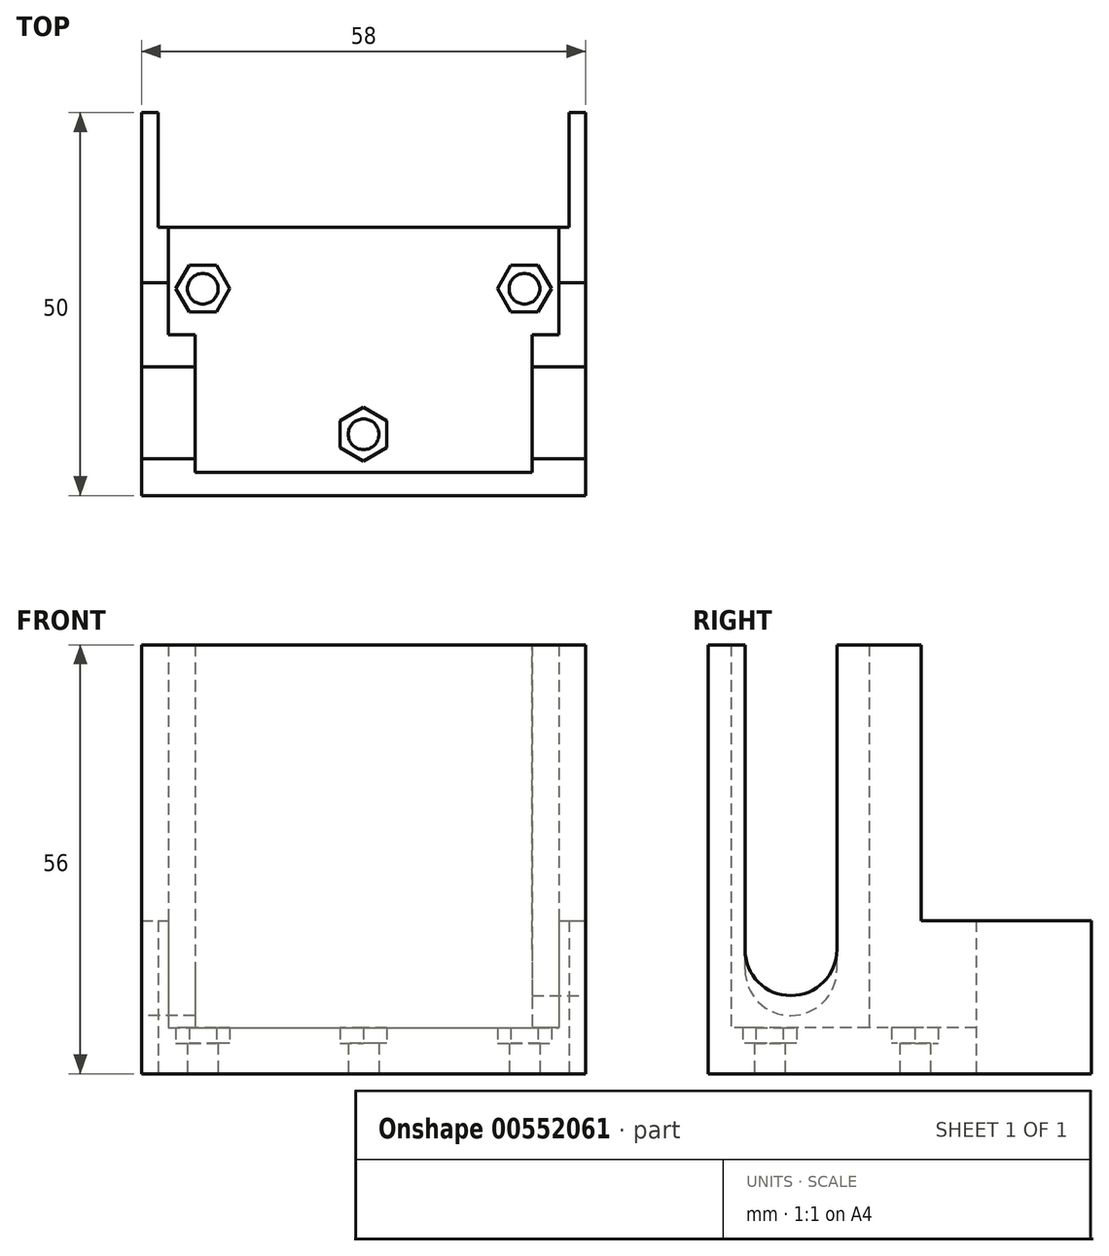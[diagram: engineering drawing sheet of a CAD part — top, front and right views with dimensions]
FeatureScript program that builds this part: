
annotation { "Feature Type Name" : "Feature", "Feature Type Description" : "" }
export const myFeature = defineFeature(function(context is Context, id is Id, definition is map)
    precondition{}
    {
        {
            var Q0;
            Q0=qCreatedBy(makeId("Top.planeOp"),FACE);
            var sketch = newSketch(context, id + "F0", { "sketchPlane" : qUnion([Q0])});
            skLineSegment(sketch, "E0.bottom", {"start": v(-26.85, 17.5) * mm, "end": v(26.85, 17.5) * mm});
            skLineSegment(sketch, "E0.top", {"start": v(-29, -17.5) * mm, "end": v(29, -17.5) * mm});
            skLineSegment(sketch, "E0.left", {"start": v(-29, 17.5) * mm, "end": v(-29, -17.5) * mm});
            skLineSegment(sketch, "E0.right", {"start": v(29, 17.5) * mm, "end": v(29, -17.5) * mm});
            skLineSegment(sketch, "E1.top", {"start": v(-29, 32.5) * mm, "end": v(-26.85, 32.5) * mm});
            skLineSegment(sketch, "E1.left", {"start": v(-29, 17.5) * mm, "end": v(-29, 32.5) * mm});
            skLineSegment(sketch, "E1.right", {"start": v(-26.85, 17.5) * mm, "end": v(-26.85, 32.5) * mm});
            skLineSegment(sketch, "E2.MirrorCS", {"start": v(29, 32.5) * mm, "end": v(26.85, 32.5) * mm});
            skLineSegment(sketch, "E3.MirrorCS", {"start": v(26.85, 17.5) * mm, "end": v(26.85, 32.5) * mm});
            skLineSegment(sketch, "E4.MirrorCS", {"start": v(29, 17.5) * mm, "end": v(29, 32.5) * mm});
            skCircle(sketch, "E5", {"center": v(-21, 9.5) * mm, "radius": 2 * mm});
            skCircle(sketch, "E6.MirrorC", {"center": v(21, 9.5) * mm, "radius": 2 * mm});
            skCircle(sketch, "E7.MirrorC", {"center": v(0, -9.5) * mm, "radius": 2 * mm});
            skSolve(sketch);
        }
        {
            var Q0;
            Q0 = qSketchRegion(id + "F0", true);
            extrude(context, id + "F1", {"entities" : qUnion([Q0]), "depth" : 4 * mm, "offsetDistance" : 25 * mm});
        }
        {
            var Q0;
            Q0=makeQuery(id+"F1.opExtrude","CAP_FACE",FACE,{"disambiguationData":[OSD([sQuery(id+"F0.wireOp",EDGE,"E0.bottom"),sQuery(id+"F0.wireOp",EDGE,"E0.top"),sQuery(id+"F0.wireOp",EDGE,"E0.left"),sQuery(id+"F0.wireOp",EDGE,"E0.right"),sQuery(id+"F0.wireOp",EDGE,"E1.top"),sQuery(id+"F0.wireOp",EDGE,"E1.left"),sQuery(id+"F0.wireOp",EDGE,"E1.right"),sQuery(id+"F0.wireOp",EDGE,"E2.MirrorCS"),sQuery(id+"F0.wireOp",EDGE,"E3.MirrorCS"),sQuery(id+"F0.wireOp",EDGE,"E4.MirrorCS"),sQuery(id+"F0.wireOp",EDGE,"E5"),sQuery(id+"F0.wireOp",EDGE,"E6.MirrorC"),sQuery(id+"F0.wireOp",EDGE,"E7.MirrorC"),sQuery(id+"F0.wireOp",EDGE,"1b375347-9f48-4c3b-9e81-8c62cc754c121.MirrorC")])],"isStart":false});
            var sketch = newSketch(context, id + "F2", { "sketchPlane" : qUnion([Q0])});
            skCircle(sketch, "E8.cCircle", {"center": v(-21, 9.5) * mm, "radius": 3.05 * mm, "construction": true});
            skLineSegment(sketch, "E8.0", {"start": v(-19.24, 6.45) * mm, "end": v(-22.76, 6.45) * mm});
            skLineSegment(sketch, "E8.1", {"start": v(-22.76, 6.45) * mm, "end": v(-24.52, 9.5) * mm});
            skLineSegment(sketch, "E8.2", {"start": v(-24.52, 9.5) * mm, "end": v(-22.76, 12.55) * mm});
            skLineSegment(sketch, "E8.3", {"start": v(-22.76, 12.55) * mm, "end": v(-19.24, 12.55) * mm});
            skLineSegment(sketch, "E8.4", {"start": v(-19.24, 12.55) * mm, "end": v(-17.48, 9.5) * mm});
            skLineSegment(sketch, "E8.5", {"start": v(-17.48, 9.5) * mm, "end": v(-19.24, 6.45) * mm});
            skPoint(sketch, "E8.0.midPoint", {"position": v(-21, 6.45) * mm});
            skLineSegment(sketch, "E9.MirrorCS", {"start": v(24.52, 9.5) * mm, "end": v(22.76, 12.55) * mm});
            skLineSegment(sketch, "E10.MirrorCS", {"start": v(17.48, 9.5) * mm, "end": v(19.24, 6.45) * mm});
            skPoint(sketch, "E11.MirrorP", {"position": v(21, 6.45) * mm});
            skCircle(sketch, "E12.MirrorC", {"center": v(21, 9.5) * mm, "radius": 3.05 * mm, "construction": true});
            skLineSegment(sketch, "E13.MirrorCS", {"start": v(19.24, 6.45) * mm, "end": v(22.76, 6.45) * mm});
            skLineSegment(sketch, "E14.MirrorCS", {"start": v(22.76, 6.45) * mm, "end": v(24.52, 9.5) * mm});
            skLineSegment(sketch, "E15.MirrorCS", {"start": v(22.76, 12.55) * mm, "end": v(19.24, 12.55) * mm});
            skLineSegment(sketch, "E16.MirrorCS", {"start": v(19.24, 12.55) * mm, "end": v(17.48, 9.5) * mm});
            skCircle(sketch, "E17.cCircle", {"center": v(0, -9.5) * mm, "radius": 3.05 * mm, "construction": true});
            skLineSegment(sketch, "E17.0", {"start": v(0, -13.02) * mm, "end": v(-3.05, -11.26) * mm});
            skLineSegment(sketch, "E17.1", {"start": v(-3.05, -11.26) * mm, "end": v(-3.05, -7.74) * mm});
            skLineSegment(sketch, "E17.2", {"start": v(-3.05, -7.74) * mm, "end": v(0, -5.98) * mm});
            skLineSegment(sketch, "E17.3", {"start": v(0, -5.98) * mm, "end": v(3.05, -7.74) * mm});
            skLineSegment(sketch, "E17.4", {"start": v(3.05, -7.74) * mm, "end": v(3.05, -11.26) * mm});
            skLineSegment(sketch, "E17.5", {"start": v(3.05, -11.26) * mm, "end": v(0, -13.02) * mm});
            skPoint(sketch, "E17.0.midPoint", {"position": v(-1.53, -12.14) * mm});
            skSolve(sketch);
        }
        {
            var Q0;
            Q0=makeQuery(id+"F2.imprint","IMPRINT",FACE,{"disambiguationData":[TD([[makeQuery(id+"F2.imprint","IMPRINT",EDGE,{"derivedFrom":sQuery(id+"F2.wireOp",EDGE,"E8.0")}),1.0]])]});
            extrude(context, id + "F3", {"entities" : qUnion([Q0]), "operationType" : NewBodyOperationType.ADD, "depth" : 2 * mm, "offsetDistance" : 25 * mm});
        }
        {
            var Q0;
            Q0=makeQuery(id+"F3.opExtrude","CAP_FACE",FACE,{"disambiguationData":[OSD([sQuery(id+"F0.wireOp",EDGE,"E0.bottom"),sQuery(id+"F0.wireOp",EDGE,"E0.top"),sQuery(id+"F0.wireOp",EDGE,"E0.left"),sQuery(id+"F0.wireOp",EDGE,"E0.right"),sQuery(id+"F0.wireOp",EDGE,"E1.top"),sQuery(id+"F0.wireOp",EDGE,"E1.left"),sQuery(id+"F0.wireOp",EDGE,"E1.right"),sQuery(id+"F0.wireOp",EDGE,"E2.MirrorCS"),sQuery(id+"F0.wireOp",EDGE,"E3.MirrorCS"),sQuery(id+"F0.wireOp",EDGE,"E4.MirrorCS"),sQuery(id+"F2.wireOp",EDGE,"E8.0"),sQuery(id+"F2.wireOp",EDGE,"E8.1"),sQuery(id+"F2.wireOp",EDGE,"E8.2"),sQuery(id+"F2.wireOp",EDGE,"E8.3"),sQuery(id+"F2.wireOp",EDGE,"E8.4"),sQuery(id+"F2.wireOp",EDGE,"E8.5"),sQuery(id+"F2.wireOp",EDGE,"E9.MirrorCS"),sQuery(id+"F2.wireOp",EDGE,"E10.MirrorCS"),sQuery(id+"F2.wireOp",EDGE,"E13.MirrorCS"),sQuery(id+"F2.wireOp",EDGE,"E14.MirrorCS"),sQuery(id+"F2.wireOp",EDGE,"E15.MirrorCS"),sQuery(id+"F2.wireOp",EDGE,"E16.MirrorCS"),sQuery(id+"F2.wireOp",EDGE,"72694715-5b62-4953-aa1a-f60ba5feefbf0.MirrorCS"),sQuery(id+"F2.wireOp",EDGE,"72694715-5b62-4953-aa1a-f60ba5feefbf1.MirrorCS"),sQuery(id+"F2.wireOp",EDGE,"72694715-5b62-4953-aa1a-f60ba5feefbf2.MirrorCS"),sQuery(id+"F2.wireOp",EDGE,"72694715-5b62-4953-aa1a-f60ba5feefbf3.MirrorCS"),sQuery(id+"F2.wireOp",EDGE,"72694715-5b62-4953-aa1a-f60ba5feefbf4.MirrorCS"),sQuery(id+"F2.wireOp",EDGE,"72694715-5b62-4953-aa1a-f60ba5feefbf8.MirrorCS"),sQuery(id+"F2.wireOp",EDGE,"72694715-5b62-4953-aa1a-f60ba5feefbf9.MirrorCS"),sQuery(id+"F2.wireOp",EDGE,"72694715-5b62-4953-aa1a-f60ba5feefbf11.MirrorCS"),sQuery(id+"F2.wireOp",EDGE,"72694715-5b62-4953-aa1a-f60ba5feefbf12.MirrorCS"),sQuery(id+"F2.wireOp",EDGE,"72694715-5b62-4953-aa1a-f60ba5feefbf13.MirrorCS"),sQuery(id+"F2.wireOp",EDGE,"72694715-5b62-4953-aa1a-f60ba5feefbf14.MirrorCS"),sQuery(id+"F2.wireOp",EDGE,"72694715-5b62-4953-aa1a-f60ba5feefbf15.MirrorCS")])],"isStart":false});
            var sketch = newSketch(context, id + "F4", { "sketchPlane" : qUnion([Q0])});
            skLineSegment(sketch, "E18", {"start": v(-25.5, 17.5) * mm, "end": v(-25.5, 3.5) * mm});
            skLineSegment(sketch, "E19.MirrorCS", {"start": v(25.5, 17.5) * mm, "end": v(25.5, 3.5) * mm});
            skLineSegment(sketch, "E20", {"start": v(-22, -14.5) * mm, "end": v(22, -14.5) * mm});
            skLineSegment(sketch, "E21.bottom", {"start": v(-25.5, 3.5) * mm, "end": v(-22, 3.5) * mm});
            skLineSegment(sketch, "E21.right", {"start": v(-22, 3.5) * mm, "end": v(-22, -14.5) * mm});
            skLineSegment(sketch, "E22.MirrorCS", {"start": v(22, 3.5) * mm, "end": v(22, -14.5) * mm});
            skLineSegment(sketch, "E23.MirrorCS", {"start": v(25.5, 3.5) * mm, "end": v(22, 3.5) * mm});
            skSolve(sketch);
        }
        {
            var Q0;
            Q0 = qSketchRegion(id + "F4", true);
            var Q1;
            {var subQ2=sQuery(id+"F4.wireOp",EDGE,"E18");Q1=makeQuery(id+"F4.imprint","IMPRINT",FACE,{"disambiguationData":[TD([[makeQuery(id+"F4.imprint","IMPRINT",EDGE,{"derivedFrom":subQ2}),-1.0]])]});}
            extrude(context, id + "F5", {"entities" : qUnion([Q0, Q1]), "operationType" : NewBodyOperationType.ADD, "depth" : 50 * mm, "offsetDistance" : 25 * mm});
        }
        {
            var Q0;
            {var subQ0=sQuery(id+"F0.wireOp",EDGE,"E1.left");var subQ1=sQuery(id+"F0.wireOp",EDGE,"E0.left");Q0=makeQuery(id+"F5.boolean.opBoolean","MERGE",FACE,{"derivedFrom":[makeQuery(id+"F3.boolean.opBoolean","MERGE",FACE,{"derivedFrom":[makeQuery(id+"F1.opExtrude","SWEPT_FACE",FACE,{"disambiguationData":[OSD([subQ1,subQ0])]}),makeQuery(id+"F3.opExtrude","SWEPT_FACE",FACE,{"disambiguationData":[OSD([subQ1,subQ0])]})]}),makeQuery(id+"F5.opExtrude","SWEPT_FACE",FACE,{"disambiguationData":[OSD([subQ1,subQ0])]})]});}
            var sketch = newSketch(context, id + "F6", { "sketchPlane" : qUnion([Q0])});
            skArc(sketch, "E24", {"start": v(0.7, 13.6) * mm, "mid": v(6.7, 7.6) * mm, "end": v(12.7, 13.6) * mm});
            skLineSegment(sketch, "E25", {"start": v(12.7, 13.6) * mm, "end": v(12.7, 56) * mm});
            skLineSegment(sketch, "E26", {"start": v(0.7, 13.6) * mm, "end": v(0.7, 56) * mm});
            skSolve(sketch);
        }
        {
            var Q0;
            Q0 = qSketchRegion(id + "F6", true);
            var Q1;
            Q1=makeQuery(id+"F6.imprint","IMPRINT",FACE,{"disambiguationData":[TD([[makeQuery(id+"F6.imprint","IMPRINT",EDGE,{"derivedFrom":sQuery(id+"F6.wireOp",EDGE,"E24")}),1.0]])]});
            extrude(context, id + "F7", {"entities" : qUnion([Q0, Q1]), "operationType" : NewBodyOperationType.REMOVE, "oppositeDirection" : true, "depth" : 8 * mm, "offsetDistance" : 25 * mm});
        }
        {
            var Q0;
            {var subQ0=sQuery(id+"F0.wireOp",EDGE,"E4.MirrorCS");var subQ1=sQuery(id+"F0.wireOp",EDGE,"E0.right");Q0=makeQuery(id+"F5.boolean.opBoolean","MERGE",FACE,{"derivedFrom":[makeQuery(id+"F3.boolean.opBoolean","MERGE",FACE,{"derivedFrom":[makeQuery(id+"F1.opExtrude","SWEPT_FACE",FACE,{"disambiguationData":[OSD([subQ1,subQ0])]}),makeQuery(id+"F3.opExtrude","SWEPT_FACE",FACE,{"disambiguationData":[OSD([subQ1,subQ0])]})]}),makeQuery(id+"F5.opExtrude","SWEPT_FACE",FACE,{"disambiguationData":[OSD([subQ1,subQ0])]})]});}
            var sketch = newSketch(context, id + "F8", { "sketchPlane" : qUnion([Q0])});
            skArc(sketch, "E27", {"start": v(-12.7, 16.2) * mm, "mid": v(-6.7, 10.2) * mm, "end": v(-0.7, 16.2) * mm});
            skLineSegment(sketch, "E28", {"start": v(-0.7, 16.2) * mm, "end": v(-0.7, 56) * mm});
            skLineSegment(sketch, "E29", {"start": v(-12.7, 16.2) * mm, "end": v(-12.7, 56) * mm});
            skSolve(sketch);
        }
        {
            var Q0;
            Q0 = qSketchRegion(id + "F8", true);
            var Q1;
            {var subQ6=sQuery(id+"F8.wireOp",EDGE,"E28");Q1=makeQuery(id+"F8.imprint","IMPRINT",FACE,{"disambiguationData":[TD([[makeQuery(id+"F8.imprint","IMPRINT",EDGE,{"derivedFrom":subQ6}),1.0]])]});}
            extrude(context, id + "F9", {"entities" : qUnion([Q0, Q1]), "operationType" : NewBodyOperationType.REMOVE, "oppositeDirection" : true, "depth" : 8 * mm, "offsetDistance" : 25 * mm});
        }
        {
            var Q0;
            {var subQ0=sQuery(id+"F0.wireOp",EDGE,"E4.MirrorCS");var subQ1=sQuery(id+"F0.wireOp",EDGE,"E0.right");Q0=makeQuery(id+"F5.boolean.opBoolean","MERGE",FACE,{"derivedFrom":[makeQuery(id+"F3.boolean.opBoolean","MERGE",FACE,{"derivedFrom":[makeQuery(id+"F1.opExtrude","SWEPT_FACE",FACE,{"disambiguationData":[OSD([subQ1,subQ0])]}),makeQuery(id+"F3.opExtrude","SWEPT_FACE",FACE,{"disambiguationData":[OSD([subQ1,subQ0])]})]}),makeQuery(id+"F5.opExtrude","SWEPT_FACE",FACE,{"disambiguationData":[OSD([subQ1,subQ0])]})]});}
            var sketch = newSketch(context, id + "F10", { "sketchPlane" : qUnion([Q0])});
            skLineSegment(sketch, "E30.bottom", {"start": v(32.5, 56) * mm, "end": v(10.3, 56) * mm});
            skLineSegment(sketch, "E30.top", {"start": v(32.5, 20) * mm, "end": v(10.3, 20) * mm});
            skLineSegment(sketch, "E30.left", {"start": v(32.5, 56) * mm, "end": v(32.5, 20) * mm});
            skLineSegment(sketch, "E30.right", {"start": v(10.3, 56) * mm, "end": v(10.3, 20) * mm});
            skSolve(sketch);
        }
        {
            var Q0;
            Q0 = qSketchRegion(id + "F10", true);
            extrude(context, id + "F11", {"entities" : qUnion([Q0]), "operationType" : NewBodyOperationType.REMOVE, "oppositeDirection" : true, "depth" : 60 * mm, "offsetDistance" : 25 * mm});
        }
    });
